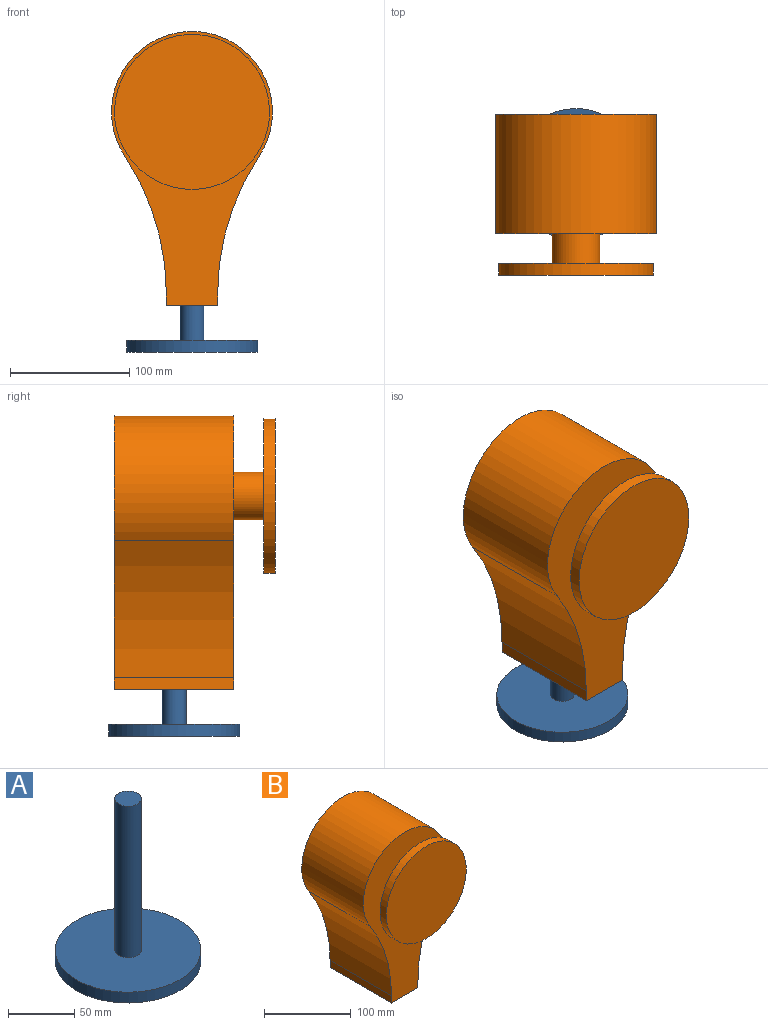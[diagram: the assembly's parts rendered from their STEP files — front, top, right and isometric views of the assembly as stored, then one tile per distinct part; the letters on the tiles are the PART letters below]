
ASSEMBLY  parts=2 mates=1
PART A: 5 faces, bbox 110x110x150 mm
  f0: cylinder r=55mm len=110mm, axis (0,0,-1), area 3455.8mm2, adj f1,f2
  f1: plane 110x110mm, normal (0,0,1), area 9189.2mm2, adj f0,f3
  f2: plane 110x110mm, normal (0,0,-1), area 9503.3mm2, adj f0
  f3: cylinder r=10mm len=140mm, axis (0,0,-1), area 8796.5mm2, adj f1,f4
  f4: plane 20x20mm, normal (0,0,1), area 314.2mm2, adj f3
PART B: 14 faces, bbox 135x135x230 mm
  f0: plane 100x10mm, normal (-1,0,0), area 1000mm2, adj f1,f5,f6,f7
  f1: plane 100x43mm, normal (0,0,-1), area 3953.6mm2, adj f0,f2,f6,f7,f12
  f2: plane 100x10mm, normal (1,0,0), area 1000mm2, adj f1,f3,f6,f7
  f3: cylinder r=208.29mm len=115.17mm, axis (0,1,0), area 12203.9mm2, adj f2,f4,f6,f7
  f4: cylinder r=67.5mm len=135mm, axis (0,1,0), area 29115.7mm2, adj f3,f5,f6,f7
  f5: cylinder r=208.29mm len=115.17mm, axis (0,1,0), area 12203.9mm2, adj f0,f4,f6,f7
  f6: plane 230x135mm, normal (0,-1,0), area 18623.3mm2, adj f0,f1,f2,f3,f4,f5,f8
  f7: plane 230x135mm, normal (0,1,0), area 19880mm2, adj f0,f1,f2,f3,f4,f5
  f8: cylinder r=20mm len=40mm, axis (0,1,0), area 3141.6mm2, adj f6,f11
  f9: cylinder r=65mm len=130mm, axis (0,1,0), area 4084.1mm2, adj f10,f11
  f10: plane 130x130mm, normal (0,-1,0), area 13273.2mm2, adj f9
  f11: plane 130x130mm, normal (0,1,0), area 12016.6mm2, adj f8,f9
  f12: cylinder r=10.5mm len=145mm, axis (0,0,-1), area 9566.1mm2, adj f1,f13
  f13: plane 21x21mm, normal (0,0,-1), area 346.4mm2, adj f12
PLACE A t=(-56.45,22.67,41.82)mm
PLACE B t=(-56.45,72.67,243.52)mm
MATE slider B.f12 <-> A.f3  axis (0,0,-1) through (-56.45,22.67,81.02)mm
